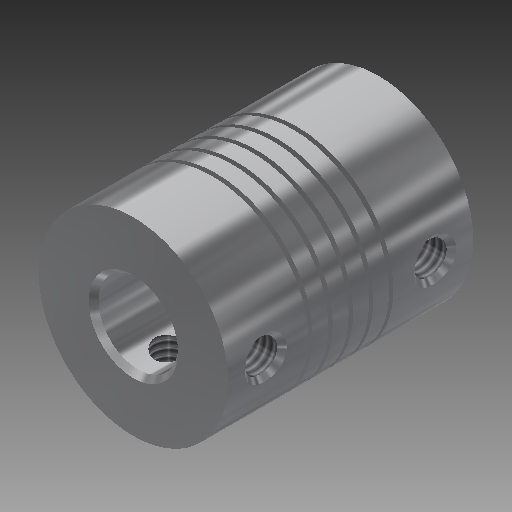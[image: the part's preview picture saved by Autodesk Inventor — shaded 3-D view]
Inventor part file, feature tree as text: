
AUTODESK INVENTOR PART (.ipt)
format: ipt  version: 2018 (Build 220112000, 112)  size: 360,960 bytes
history: native  units: in
note: dims shown in document units (in); Inventor stores cm internally (conversion verified against a paired STEP export)
features: sketch x5, extrude x2, hole x2, chamfer x2, helix x1, plane x1, other x1
ambient origin geometry x8: Origin, YZ Plane, XZ Plane, XY Plane, X Axis, Y Axis, Z Axis, Center Point
bodies: Solid1 (feature_tree)
feature tree (14):
  sketch  "Sketch1"  dims[d0=0.75in d1=0.1969in]
  extrude  "Extrusion1"  Depth=0.1969in
  extrude  "Extrusion2"  Depth=0.315in
  helix  "Coil1"  [1 undecoded]
  hole  "Hole1"  [1 undecoded]
  plane  "Work Plane2"
  hole  "Hole2"  [1 undecoded]
  chamfer  "Chamfer1"  Distance=0.1575in
  chamfer  "Chamfer2"  Distance=0.15in
  sketch  "Sketch3"  dims[d2=0.97in d3=0.0in d4=0.315in d5=0.69in d6=0.0in]
  sketch  "Sketch5"  dims[d8=0.017in]
  sketch  "Sketch6"  dims[d9=0.08in d10=1.0in d11=1.9685in d12=0.0in d13=90.0deg d14=90.0deg d15=0.0in d16=0.0in d17=0.277in]
  other  "Work Axis1"
  sketch  "Sketch8"  dims[d18=0.1575in d19=0.15in d20=0.1575in d21=0.15in d22=0.128in d23=0.75in d24=0.375in d25=0.25in d26=0.5635in d27=1.0in d28=0.8108in d29=90.0deg d30=0.1575in d31=0.1575in d32=0.15in d33=0.1496in d34=0.128in d35=0.75in d36=0.375in d37=0.25in d38=0.5635in d39=1.0in d40=0.8108in d41=0.0197in d42=0.125in d43=45.0deg d44=0.0197in d45=0.125in d46=45.0deg]
note: 3 required parameter values undecoded (feature->parameter linkage not recoverable at this tier; creation-order binding heuristic only, values carry confidence <= 0.55)
